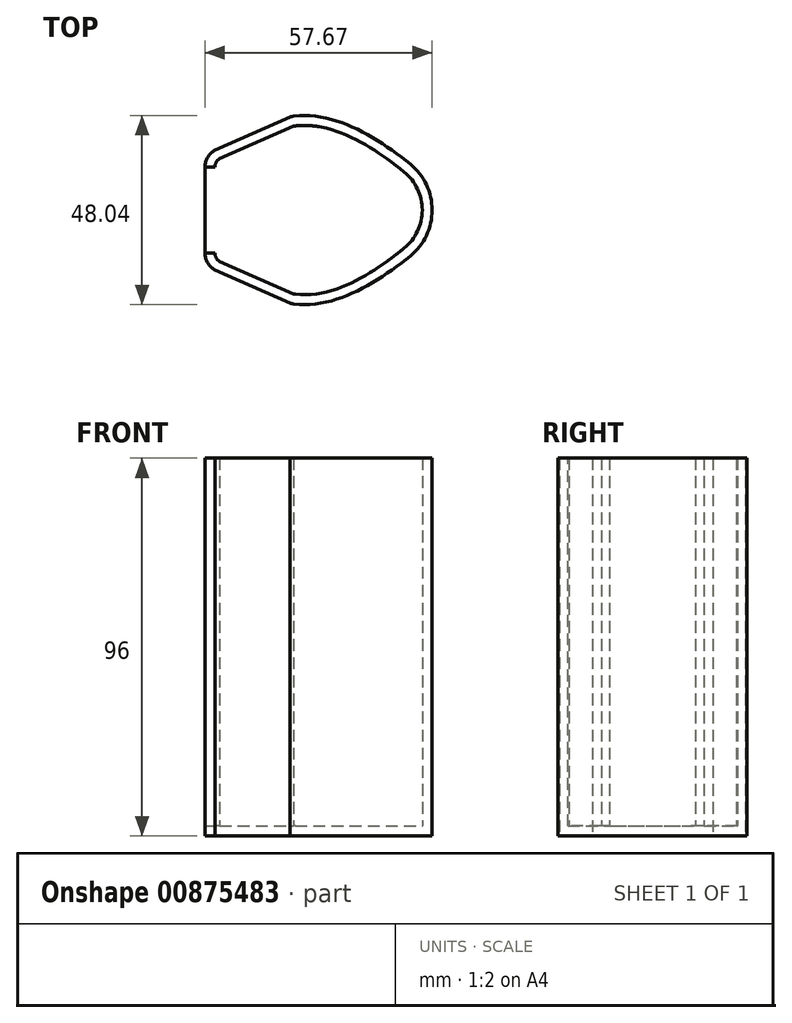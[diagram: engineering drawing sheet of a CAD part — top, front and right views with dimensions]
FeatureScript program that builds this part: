
annotation { "Feature Type Name" : "Feature", "Feature Type Description" : "" }
export const myFeature = defineFeature(function(context is Context, id is Id, definition is map)
    precondition{}
    {
        {
            var Q0;
            Q0=qCreatedBy(makeId("Top.planeOp"),FACE);
            var sketch = newSketch(context, id + "F0", { "sketchPlane" : qUnion([Q0])});
            skLineSegment(sketch, "E0", {"start": v(-23.49, 0) * mm, "end": v(-23.49, 10.9) * mm});
            skPoint(sketch, "E1.visualSharp", {"position": v(-23.49, 15) * mm});
            skArc(sketch, "E1.filletArc", {"start": v(-20.91, 15.27) * mm, "mid": v(-22.8, 13.44) * mm, "end": v(-23.49, 10.9) * mm});
            skPoint(sketch, "E2.visualSharp", {"position": v(0, 24.2) * mm});
            skArc(sketch, "E2.filletArc", {"start": v(-0.85, 23.88) * mm, "mid": v(-1.39, 23.78) * mm, "end": v(-1.91, 23.63) * mm});
            skPoint(sketch, "E3.visualSharp", {"position": v(41.44, 0) * mm});
            skFitSpline(sketch, "E4", {"points": [v(-0.85, 23.88) * mm, v(41.44, 0) * mm], "startDerivative": vector(49.53, 5.83) * mm, "endDerivative": vector(25.26, -24) * mm});
            skFitSpline(sketch, "E5.MirrorCS", {"points": [v(-0.85, -23.88) * mm, v(41.44, 0) * mm], "startDerivative": vector(49.53, -5.83) * mm, "endDerivative": vector(25.26, 24) * mm});
            skPoint(sketch, "E6.MirrorP", {"position": v(0, -24.2) * mm});
            skArc(sketch, "E7.MirrorCS", {"start": v(-0.85, -23.88) * mm, "mid": v(-1.39, -23.78) * mm, "end": v(-1.91, -23.63) * mm});
            skArc(sketch, "E8.MirrorCS", {"start": v(-20.91, -15.27) * mm, "mid": v(-22.8, -13.44) * mm, "end": v(-23.49, -10.9) * mm});
            skLineSegment(sketch, "E9.MirrorCS", {"start": v(-23.49, 0) * mm, "end": v(-23.49, -10.9) * mm});
            skArc(sketch, "E10.filletArc", {"start": v(28.65, -11.64) * mm, "mid": v(34.18, 0) * mm, "end": v(28.65, 11.64) * mm});
            skLineSegment(sketch, "E11", {"start": v(-20.91, 15.27) * mm, "end": v(-1.91, 23.63) * mm});
            skLineSegment(sketch, "E12.MirrorCS", {"start": v(-20.91, -15.27) * mm, "end": v(-1.91, -23.63) * mm});
            skSolve(sketch);
        }
        {
            var Q0;
            Q0=makeQuery(id+"F0.imprint","IMPRINT",FACE,{"disambiguationData":[TD([[makeQuery(id+"F0.imprint","IMPRINT",EDGE,{"derivedFrom":sQuery(id+"F0.wireOp",EDGE,"E0")}),-1.0]])]});
            extrude(context, id + "F1", {"entities" : qUnion([Q0]), "depth" : 96 * mm, "offsetDistance" : 25 * mm});
        }
        {
            var Q0;
            Q0=makeQuery(id+"F1.opExtrude","CAP_FACE",FACE,{"disambiguationData":[OSD([sQuery(id+"F0.wireOp",EDGE,"E0"),sQuery(id+"F0.wireOp",EDGE,"E1.filletArc"),sQuery(id+"F0.wireOp",EDGE,"E2.filletArc"),sQuery(id+"F0.wireOp",EDGE,"E4"),sQuery(id+"F0.wireOp",EDGE,"E5.MirrorCS"),sQuery(id+"F0.wireOp",EDGE,"E7.MirrorCS"),sQuery(id+"F0.wireOp",EDGE,"E8.MirrorCS"),sQuery(id+"F0.wireOp",EDGE,"E9.MirrorCS"),sQuery(id+"F0.wireOp",EDGE,"E10.filletArc"),sQuery(id+"F0.wireOp",EDGE,"E11"),sQuery(id+"F0.wireOp",EDGE,"E12.MirrorCS")])],"isStart":false});
            var Q1;
            Q1=makeQuery(id+"F1.opExtrude","SWEPT_FACE",FACE,{"disambiguationData":[OSD([sQuery(id+"F0.wireOp",EDGE,"E0"),sQuery(id+"F0.wireOp",EDGE,"E9.MirrorCS")])]});
            shell(context, id + "F2", {"entities" : qUnion([Q0, Q1]), "thickness" : 2.5 * mm});
        }
    });
